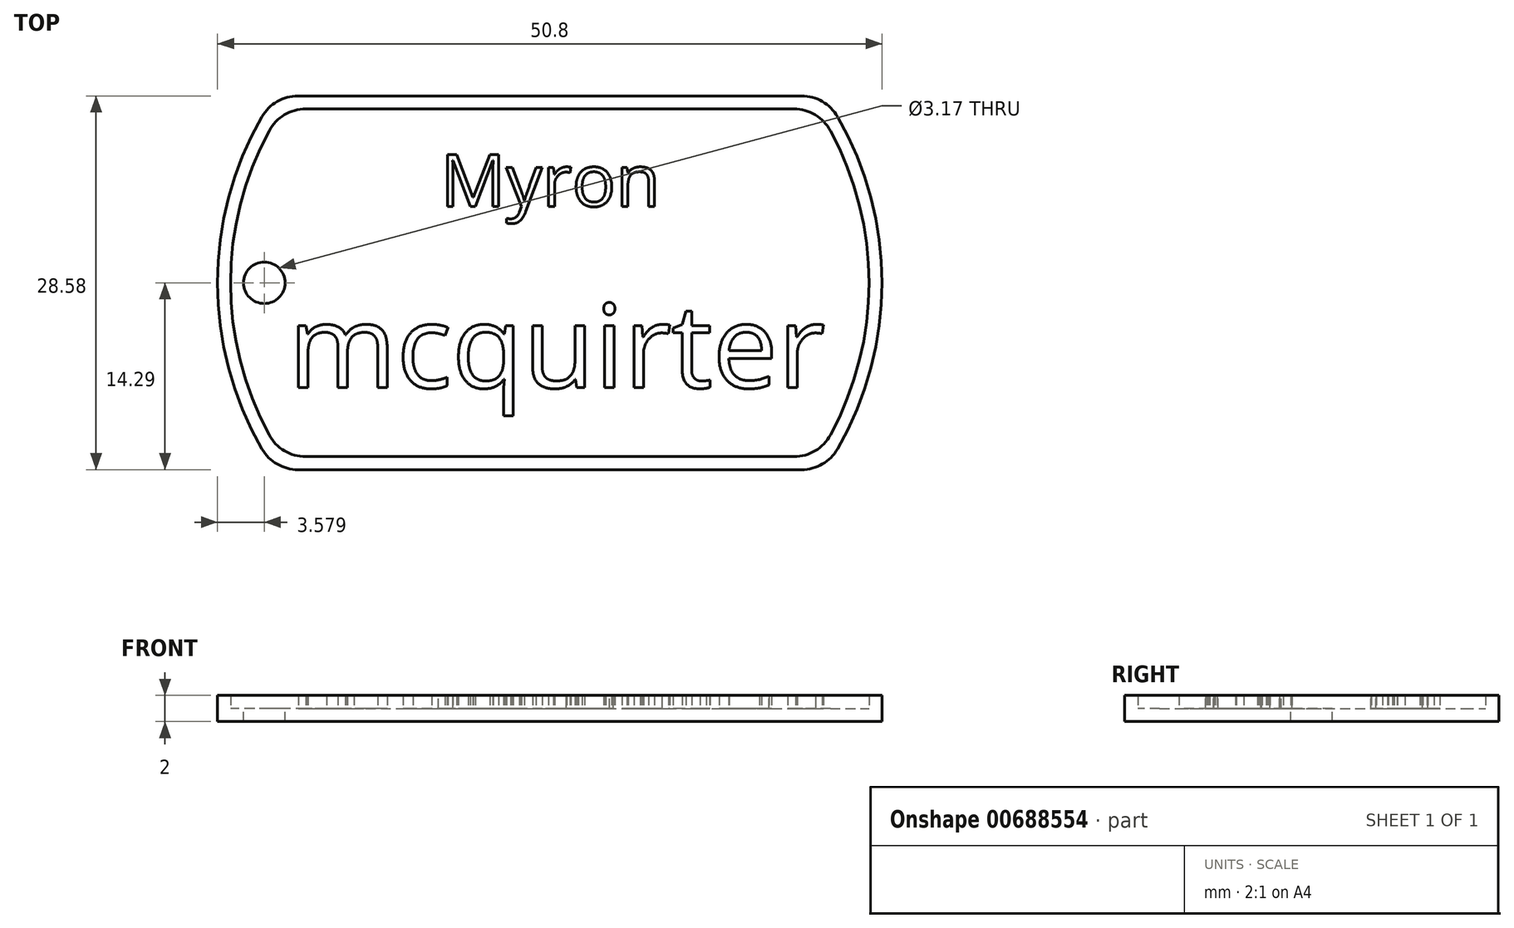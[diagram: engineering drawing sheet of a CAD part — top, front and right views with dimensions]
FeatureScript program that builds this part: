
annotation { "Feature Type Name" : "Feature", "Feature Type Description" : "" }
export const myFeature = defineFeature(function(context is Context, id is Id, definition is map)
    precondition{}
    {
        {
            var Q0;
            Q0=qCreatedBy(makeId("Top.planeOp"),FACE);
            var sketch = newSketch(context, id + "F0", { "sketchPlane" : qUnion([Q0])});
            skArc(sketch, "E0", {"start": v(-22, 12.7) * mm, "mid": v(-25.4, 0) * mm, "end": v(-22, -12.7) * mm});
            skLineSegment(sketch, "E1.top", {"start": v(-19.25, -14.29) * mm, "end": v(19.25, -14.29) * mm});
            skArc(sketch, "E2.trimOffspring", {"start": v(22, -12.7) * mm, "mid": v(25.4, 0) * mm, "end": v(22, 12.7) * mm});
            skLineSegment(sketch, "E3", {"start": v(-19.25, 14.29) * mm, "end": v(19.25, 14.29) * mm});
            skPoint(sketch, "E4.visualSharp", {"position": v(-21, 14.29) * mm});
            skArc(sketch, "E4.filletArc", {"start": v(-19.25, 14.29) * mm, "mid": v(-20.83, 13.86) * mm, "end": v(-22, 12.7) * mm});
            skPoint(sketch, "E5.visualSharp", {"position": v(21, 14.29) * mm});
            skArc(sketch, "E5.filletArc", {"start": v(22, 12.7) * mm, "mid": v(20.83, 13.86) * mm, "end": v(19.25, 14.29) * mm});
            skPoint(sketch, "E6.visualSharp", {"position": v(21, -14.29) * mm});
            skArc(sketch, "E6.filletArc", {"start": v(19.25, -14.29) * mm, "mid": v(20.83, -13.86) * mm, "end": v(22, -12.7) * mm});
            skPoint(sketch, "E7.visualSharp", {"position": v(-21, -14.29) * mm});
            skArc(sketch, "E7.filletArc", {"start": v(-22, -12.7) * mm, "mid": v(-20.83, -13.86) * mm, "end": v(-19.25, -14.29) * mm});
            skSolve(sketch);
        }
        {
            var Q0;
            Q0=makeQuery(id+"F0.imprint","IMPRINT",FACE,{"disambiguationData":[TD([[makeQuery(id+"F0.imprint","IMPRINT",EDGE,{"derivedFrom":sQuery(id+"F0.wireOp",EDGE,"E0")}),1.0]])]});
            extrude(context, id + "F1", {"entities" : qUnion([Q0]), "depth" : 1 * mm, "offsetDistance" : 25.4 * mm});
        }
        {
            var Q0;
            Q0=makeQuery(id+"F1.opExtrude","CAP_FACE",FACE,{"disambiguationData":[OSD([sQuery(id+"F0.wireOp",EDGE,"E0"),sQuery(id+"F0.wireOp",EDGE,"E1.top"),sQuery(id+"F0.wireOp",EDGE,"E2.trimOffspring"),sQuery(id+"F0.wireOp",EDGE,"E3"),sQuery(id+"F0.wireOp",EDGE,"E4.filletArc"),sQuery(id+"F0.wireOp",EDGE,"E5.filletArc"),sQuery(id+"F0.wireOp",EDGE,"E6.filletArc"),sQuery(id+"F0.wireOp",EDGE,"E7.filletArc")])],"isStart":false});
            var sketch = newSketch(context, id + "F2", { "sketchPlane" : qUnion([Q0])});
            skLineSegment(sketch, "E8.0", {"start": v(-18.66, 13.29) * mm, "end": v(18.66, 13.29) * mm});
            skArc(sketch, "E8.1", {"start": v(-21.45, 11.63) * mm, "mid": v(-24.4, 0) * mm, "end": v(-21.45, -11.63) * mm});
            skLineSegment(sketch, "E8.2", {"start": v(-18.66, -13.29) * mm, "end": v(18.66, -13.29) * mm});
            skArc(sketch, "E8.3", {"start": v(21.45, -11.63) * mm, "mid": v(24.4, 0) * mm, "end": v(21.45, 11.63) * mm});
            skPoint(sketch, "E9.visualSharp", {"position": v(-20.46, 13.29) * mm});
            skArc(sketch, "E9.filletArc", {"start": v(-18.66, 13.29) * mm, "mid": v(-20.29, 12.84) * mm, "end": v(-21.45, 11.63) * mm});
            skPoint(sketch, "E10.visualSharp", {"position": v(20.46, 13.29) * mm});
            skArc(sketch, "E10.filletArc", {"start": v(21.45, 11.63) * mm, "mid": v(20.29, 12.84) * mm, "end": v(18.66, 13.29) * mm});
            skPoint(sketch, "E11.visualSharp", {"position": v(20.46, -13.29) * mm});
            skArc(sketch, "E11.filletArc", {"start": v(18.66, -13.29) * mm, "mid": v(20.29, -12.84) * mm, "end": v(21.45, -11.63) * mm});
            skPoint(sketch, "E12.visualSharp", {"position": v(-20.46, -13.29) * mm});
            skArc(sketch, "E12.filletArc", {"start": v(-21.45, -11.63) * mm, "mid": v(-20.29, -12.84) * mm, "end": v(-18.66, -13.29) * mm});
            skLineSegment(sketch, "E13.0", {"start": v(-19.25, 14.29) * mm, "end": v(19.25, 14.29) * mm});
            skArc(sketch, "E13.1", {"start": v(-22, 12.7) * mm, "mid": v(-25.4, 0) * mm, "end": v(-22, -12.7) * mm});
            skLineSegment(sketch, "E13.2", {"start": v(-19.25, -14.29) * mm, "end": v(19.25, -14.29) * mm});
            skArc(sketch, "E13.3", {"start": v(22, -12.7) * mm, "mid": v(25.4, 0) * mm, "end": v(22, 12.7) * mm});
            skPoint(sketch, "E14.visualSharp", {"position": v(-21, -14.29) * mm});
            skArc(sketch, "E14.filletArc", {"start": v(-22, -12.7) * mm, "mid": v(-20.83, -13.86) * mm, "end": v(-19.25, -14.29) * mm});
            skPoint(sketch, "E15.visualSharp", {"position": v(21, -14.29) * mm});
            skArc(sketch, "E15.filletArc", {"start": v(19.25, -14.29) * mm, "mid": v(20.83, -13.86) * mm, "end": v(22, -12.7) * mm});
            skPoint(sketch, "E16.visualSharp", {"position": v(21, 14.29) * mm});
            skArc(sketch, "E16.filletArc", {"start": v(22, 12.7) * mm, "mid": v(20.83, 13.86) * mm, "end": v(19.25, 14.29) * mm});
            skPoint(sketch, "E17.visualSharp", {"position": v(-21, 14.29) * mm});
            skArc(sketch, "E17.filletArc", {"start": v(-19.25, 14.29) * mm, "mid": v(-20.83, 13.86) * mm, "end": v(-22, 12.7) * mm});
            skSolve(sketch);
        }
        {
            var Q0;
            Q0=makeQuery(id+"F2.imprint","IMPRINT",FACE,{"disambiguationData":[TD([[makeQuery(id+"F2.imprint","IMPRINT",EDGE,{"derivedFrom":sQuery(id+"F2.wireOp",EDGE,"E8.0")}),1.0]])]});
            extrude(context, id + "F3", {"entities" : qUnion([Q0]), "operationType" : NewBodyOperationType.ADD, "depth" : 1 * mm, "offsetDistance" : 25.4 * mm});
        }
        {
            var Q0;
            Q0=makeQuery(id+"F1.opExtrude","CAP_FACE",FACE,{"disambiguationData":[OSD([sQuery(id+"F0.wireOp",EDGE,"E0"),sQuery(id+"F0.wireOp",EDGE,"E1.top"),sQuery(id+"F0.wireOp",EDGE,"E2.trimOffspring"),sQuery(id+"F0.wireOp",EDGE,"E3"),sQuery(id+"F0.wireOp",EDGE,"E4.filletArc"),sQuery(id+"F0.wireOp",EDGE,"E5.filletArc"),sQuery(id+"F0.wireOp",EDGE,"E6.filletArc"),sQuery(id+"F0.wireOp",EDGE,"E7.filletArc")])],"isStart":false});
            var sketch = newSketch(context, id + "F4", { "sketchPlane" : qUnion([Q0])});
            skCircle(sketch, "E18", {"center": v(-21.82, 0) * mm, "radius": 1.59 * mm});
            skSolve(sketch);
        }
        {
            var Q0;
            Q0=makeQuery(id+"F4.imprint","IMPRINT",FACE,{"disambiguationData":[TD([[makeQuery(id+"F4.imprint","IMPRINT",EDGE,{"derivedFrom":sQuery(id+"F4.wireOp",EDGE,"E18")}),1.0]])]});
            extrude(context, id + "F5", {"entities" : qUnion([Q0]), "operationType" : NewBodyOperationType.REMOVE, "oppositeDirection" : true, "depth" : 1 * mm, "offsetDistance" : 25.4 * mm});
        }
        {
            var Q0;
            Q0=makeQuery(id+"F2.imprint","IMPRINT",FACE,{"disambiguationData":[TD([[makeQuery(id+"F2.imprint","IMPRINT",EDGE,{"derivedFrom":sQuery(id+"F2.wireOp",EDGE,"E8.0")}),-1.0]])]});
            var sketch = newSketch(context, id + "F6", { "sketchPlane" : qUnion([Q0])});
            skText(sketch, "E19", { "text": "Myron", "fontName": "OpenSans-Regular.ttf"});
            const initialGuessF6  = {"E19": [-0.00836, 0.00585, 1, 0, 0.00399]};
            skSetInitialGuess(sketch, initialGuessF6);
            skSolve(sketch);
        }
        {
            var Q0;
            Q0=makeQuery(id+"F6.imprint","IMPRINT",FACE,{"disambiguationData":[TD([[makeQuery(id+"F6.imprint","IMPRINT",EDGE,{"derivedFrom":sQuery(id+"F6.wireOp",EDGE,"E19.sketch_text.stroke-0")}),1.0]])]});
            var sketch = newSketch(context, id + "F7", { "sketchPlane" : qUnion([Q0])});
            skText(sketch, "E20", { "text": "mcquirter", "fontName": "OpenSans-Regular.ttf"});
            const initialGuessF7  = {"E20": [-0.01998, -0.00802, 1, 0, 0.0064]};
            skSetInitialGuess(sketch, initialGuessF7);
            skSolve(sketch);
        }
        {
            var Q0;
            Q0 = qSketchRegion(id + "F6", true);
            extrude(context, id + "F8", {"entities" : qUnion([Q0]), "operationType" : NewBodyOperationType.ADD, "depth" : 1 * mm, "offsetDistance" : 25.4 * mm});
        }
        {
            var Q0;
            Q0 = qSketchRegion(id + "F7", true);
            extrude(context, id + "F9", {"entities" : qUnion([Q0]), "operationType" : NewBodyOperationType.ADD, "depth" : 1 * mm, "offsetDistance" : 25.4 * mm});
        }
    });
